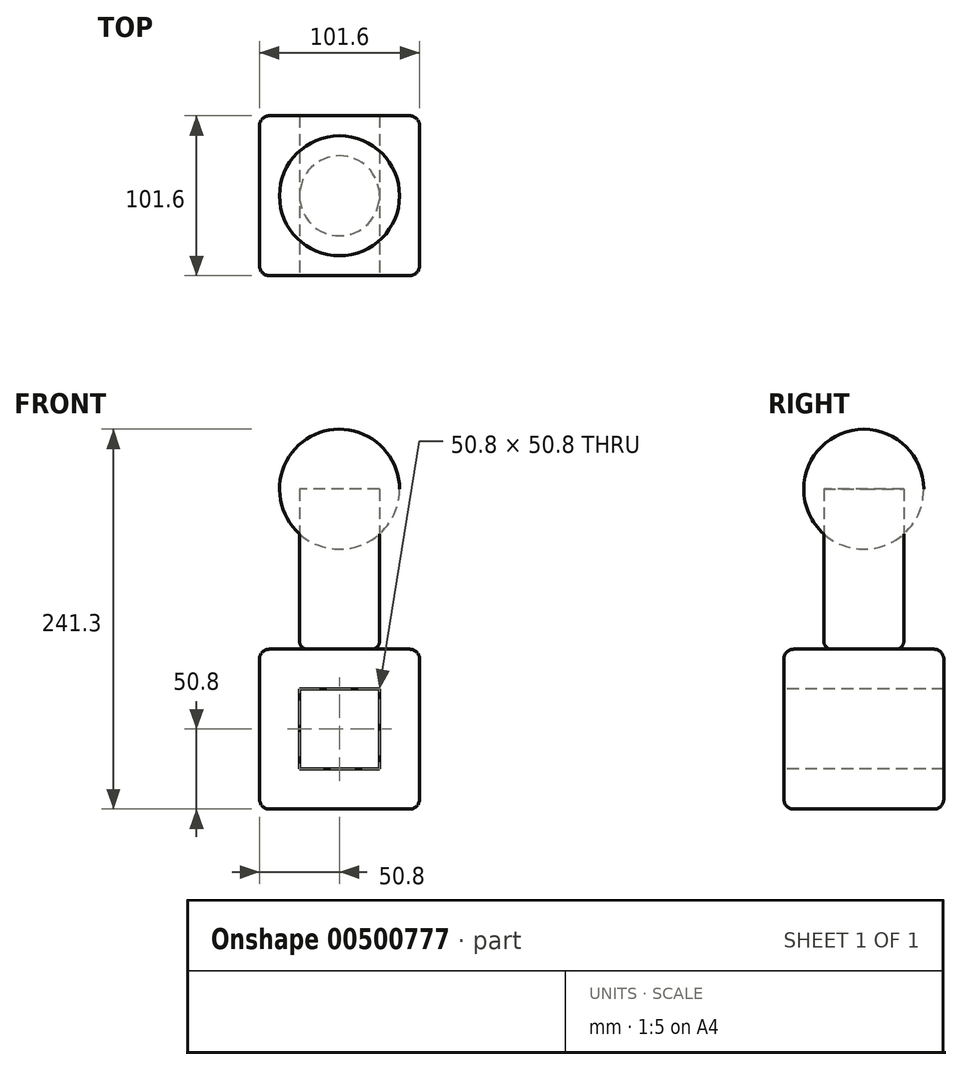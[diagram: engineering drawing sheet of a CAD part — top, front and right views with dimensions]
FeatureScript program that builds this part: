
annotation { "Feature Type Name" : "Feature", "Feature Type Description" : "" }
export const myFeature = defineFeature(function(context is Context, id is Id, definition is map)
    precondition{}
    {
        {
            var Q0;
            Q0=qCreatedBy(makeId("Top.planeOp"),FACE);
            var sketch = newSketch(context, id + "F0", { "sketchPlane" : qUnion([Q0])});
            skLineSegment(sketch, "E0.bottom", {"start": v(50.8, -50.8) * mm, "end": v(-50.8, -50.8) * mm});
            skLineSegment(sketch, "E0.top", {"start": v(50.8, 50.8) * mm, "end": v(-50.8, 50.8) * mm});
            skLineSegment(sketch, "E0.left", {"start": v(50.8, -50.8) * mm, "end": v(50.8, 50.8) * mm});
            skLineSegment(sketch, "E0.right", {"start": v(-50.8, -50.8) * mm, "end": v(-50.8, 50.8) * mm});
            skPoint(sketch, "E0.middle", {"position": v(0, 0) * mm});
            skSolve(sketch);
        }
        {
            var Q0;
            Q0=makeQuery(id+"F0.imprint","IMPRINT",FACE,{"disambiguationData":[TD([[makeQuery(id+"F0.imprint","IMPRINT",EDGE,{"derivedFrom":sQuery(id+"F0.wireOp",EDGE,"E0.bottom")}),-1.0]])]});
            extrude(context, id + "F1", {"entities" : qUnion([Q0]), "depth" : 101.6 * mm});
        }
        {
            var Q0;
            Q0=makeQuery(id+"F1.opExtrude","CAP_FACE",FACE,{"disambiguationData":[OSD([sQuery(id+"F0.wireOp",EDGE,"E0.bottom"),sQuery(id+"F0.wireOp",EDGE,"E0.top"),sQuery(id+"F0.wireOp",EDGE,"E0.left"),sQuery(id+"F0.wireOp",EDGE,"E0.right")])],"isStart":false});
            var sketch = newSketch(context, id + "F2", { "sketchPlane" : qUnion([Q0])});
            skCircle(sketch, "E1", {"center": v(0, 0) * mm, "radius": 25.4 * mm});
            skSolve(sketch);
        }
        {
            var Q0;
            Q0=makeQuery(id+"F2.imprint","IMPRINT",FACE,{"disambiguationData":[TD([[makeQuery(id+"F2.imprint","IMPRINT",EDGE,{"derivedFrom":sQuery(id+"F2.wireOp",EDGE,"E1")}),1.0]])]});
            extrude(context, id + "F3", {"entities" : qUnion([Q0]), "depth" : 101.6 * mm});
        }
        {
            var Q0;
            Q0=makeQuery(id+"F3.opExtrude","CAP_FACE",FACE,{"disambiguationData":[OSD([sQuery(id+"F2.wireOp",EDGE,"E1")])],"isStart":false});
            var sketch = newSketch(context, id + "F4", { "sketchPlane" : qUnion([Q0])});
            skArc(sketch, "E2", {"start": v(0, -38.1) * mm, "mid": v(38.1, 0) * mm, "end": v(0, 38.1) * mm});
            skLineSegment(sketch, "E3", {"start": v(0, 38.1) * mm, "end": v(0, -38.1) * mm});
            skSolve(sketch);
        }
        {
            var Q0;
            {var subQ0=sQuery(id+"F4.wireOp",EDGE,"E2");Q0=makeQuery(id+"F4.imprint","IMPRINT",FACE,{"disambiguationData":[TD([[makeQuery(id+"F4.imprint","IMPRINT",EDGE,{"derivedFrom":subQ0}),1.0]])]});}
            var Q1;
            {var subQ0=sQuery(id+"F4.wireOp",EDGE,"E3");var subQ1=makeQuery(id+"F3.opExtrude","CAP_EDGE",EDGE,{"disambiguationData":[OSD([sQuery(id+"F2.wireOp",EDGE,"E1")])],"isStart":false});var subQ2=makeQuery(id+"F4.imprint","INTERSECT",VERTEX,{"disambiguationData":[OD(0.0)],"derivedFrom":[subQ1,subQ0]});Q1=makeQuery(id+"F4.imprint","IMPRINT",FACE,{"disambiguationData":[TD([[makeQuery(id+"F4.imprint","IMPRINT",EDGE,{"disambiguationData":[TD([[subQ2,-1.0]])],"derivedFrom":subQ0}),1.0]])]});}
            var Q2;
            Q2=sQuery(id+"F4.wireOp",EDGE,"E3");
            revolve(context, id + "F5", {"entities" : qUnion([Q0, Q1]), "axis" : qUnion([Q2]), "revolveType" : RevolveType.FULL});
        }
        {
            var Q0;
            Q0=makeQuery(id+"F1.opExtrude","SWEPT_FACE",FACE,{"disambiguationData":[OSD([sQuery(id+"F0.wireOp",EDGE,"E0.bottom")])]});
            var sketch = newSketch(context, id + "F6", { "sketchPlane" : qUnion([Q0])});
            skLineSegment(sketch, "E4.bottom", {"start": v(25.4, 25.4) * mm, "end": v(-25.4, 25.4) * mm});
            skLineSegment(sketch, "E4.top", {"start": v(25.4, 76.2) * mm, "end": v(-25.4, 76.2) * mm});
            skLineSegment(sketch, "E4.left", {"start": v(25.4, 25.4) * mm, "end": v(25.4, 76.2) * mm});
            skLineSegment(sketch, "E4.right", {"start": v(-25.4, 25.4) * mm, "end": v(-25.4, 76.2) * mm});
            skPoint(sketch, "E4.middle", {"position": v(0, 50.8) * mm});
            skPoint(sketch, "E4.middle.positionSnap0", {"position": v(50.8, 50.8) * mm});
            skPoint(sketch, "E4.centerSnap0", {"position": v(50.8, 50.8) * mm});
            skSolve(sketch);
        }
        {
            var Q0;
            Q0=makeQuery(id+"F6.imprint","IMPRINT",FACE,{"disambiguationData":[TD([[makeQuery(id+"F6.imprint","IMPRINT",EDGE,{"derivedFrom":sQuery(id+"F6.wireOp",EDGE,"E4.bottom")}),-1.0]])]});
            extrude(context, id + "F7", {"entities" : qUnion([Q0]), "operationType" : NewBodyOperationType.REMOVE, "oppositeDirection" : true, "depth" : 101.6 * mm});
        }
        {
            var Q0;
            Q0=makeQuery(id+"F1.opExtrude","CAP_EDGE",EDGE,{"disambiguationData":[OSD([sQuery(id+"F0.wireOp",EDGE,"E0.left")])],"isStart":false});
            var Q1;
            Q1=makeQuery(id+"F1.opExtrude","CAP_EDGE",EDGE,{"disambiguationData":[OSD([sQuery(id+"F0.wireOp",EDGE,"E0.bottom")])],"isStart":false});
            var Q2;
            Q2=makeQuery(id+"F1.opExtrude","CAP_EDGE",EDGE,{"disambiguationData":[OSD([sQuery(id+"F0.wireOp",EDGE,"E0.right")])],"isStart":false});
            var Q3;
            Q3=makeQuery(id+"F1.opExtrude","CAP_EDGE",EDGE,{"disambiguationData":[OSD([sQuery(id+"F0.wireOp",EDGE,"E0.top")])],"isStart":false});
            var Q4;
            Q4=makeQuery(id+"F1.opExtrude","CAP_EDGE",EDGE,{"disambiguationData":[OSD([sQuery(id+"F0.wireOp",EDGE,"E0.left")])],"isStart":true});
            var Q5;
            Q5=makeQuery(id+"F1.opExtrude","SWEPT_EDGE",EDGE,{"disambiguationData":[OSD([sQuery(id+"F0.wireOp",EDGE,"E0.top"),sQuery(id+"F0.wireOp",EDGE,"E0.left")])]});
            var Q6;
            Q6=makeQuery(id+"F1.opExtrude","SWEPT_EDGE",EDGE,{"disambiguationData":[OSD([sQuery(id+"F0.wireOp",EDGE,"E0.bottom"),sQuery(id+"F0.wireOp",EDGE,"E0.left")])]});
            var Q7;
            Q7=makeQuery(id+"F1.opExtrude","SWEPT_EDGE",EDGE,{"disambiguationData":[OSD([sQuery(id+"F0.wireOp",EDGE,"E0.bottom"),sQuery(id+"F0.wireOp",EDGE,"E0.right")])]});
            var Q8;
            Q8=makeQuery(id+"F1.opExtrude","CAP_EDGE",EDGE,{"disambiguationData":[OSD([sQuery(id+"F0.wireOp",EDGE,"E0.bottom")])],"isStart":true});
            var Q9;
            Q9=makeQuery(id+"F1.opExtrude","CAP_EDGE",EDGE,{"disambiguationData":[OSD([sQuery(id+"F0.wireOp",EDGE,"E0.right")])],"isStart":true});
            var Q10;
            Q10=makeQuery(id+"F1.opExtrude","CAP_EDGE",EDGE,{"disambiguationData":[OSD([sQuery(id+"F0.wireOp",EDGE,"E0.top")])],"isStart":true});
            var Q11;
            Q11=makeQuery(id+"F1.opExtrude","SWEPT_EDGE",EDGE,{"disambiguationData":[OSD([sQuery(id+"F0.wireOp",EDGE,"E0.top"),sQuery(id+"F0.wireOp",EDGE,"E0.right")])]});
            fillet(context, id + "F8", {"entities" : qUnion([Q0, Q1, Q2, Q3, Q4, Q5, Q6, Q7, Q8, Q9, Q10, Q11]), "radius" : 6.35 * mm, "tangentPropagation" : true, "allowEdgeOverflow" : false});
        }
        {
            var Q0;
            Q0=makeQuery(id+"F3.opExtrude","CAP_EDGE",EDGE,{"disambiguationData":[OSD([sQuery(id+"F2.wireOp",EDGE,"E1")])],"isStart":true});
            fillet(context, id + "F9", {"entities" : qUnion([Q0]), "radius" : 5.08 * mm, "tangentPropagation" : true, "allowEdgeOverflow" : false});
        }
    });
